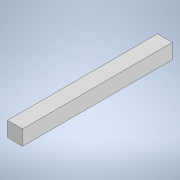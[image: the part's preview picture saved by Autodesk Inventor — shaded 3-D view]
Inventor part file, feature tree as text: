
AUTODESK INVENTOR PART (.ipt)
format: ipt  version: 2020.1 (Build 241239000, 239)  size: 91,648 bytes
history: native  units: in
note: dims shown in document units (in); Inventor stores cm internally (conversion verified against a paired STEP export)
features: extrude x1, sketch x1
ambient origin geometry x8: Origin, YZ Plane, XZ Plane, XY Plane, X Axis, Y Axis, Z Axis, Center Point
bodies: Solid1 (feature_tree)
feature tree (2):
  extrude  "Extrusion1"  Depth=0.2362in
  sketch  "Sketch1"  dims[d0=0.2362in d1=0.2362in d2=2.3622in d3=0.0in]
